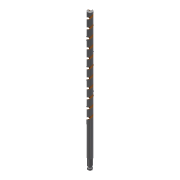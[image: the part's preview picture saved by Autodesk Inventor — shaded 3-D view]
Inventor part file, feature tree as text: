
AUTODESK INVENTOR PART (.ipt)
format: ipt  version: 2014 SP1 (Build 180222100, 222)  size: 258,048 bytes
history: native  units: in
note: dims shown in document units (in); Inventor stores cm internally (conversion verified against a paired STEP export)
features: sketch x6, extrude x4, fillet x1, helix x1
ambient origin geometry x8: Origin, YZ Plane, XZ Plane, XY Plane, X Axis, Y Axis, Z Axis, Center Point
bodies: Solid1 (feature_tree)
feature tree (12):
  extrude  "Extrusion1"  Depth=0.21in TaperAngle=0.0deg
  extrude  "Extrusion2"  Depth=0.1805in TaperAngle=0.0deg
  extrude  "Extrusion3"  Depth=0.89in TaperAngle=0.0deg
  fillet  "Fillet1"  Radius=0.05in
  extrude  "Extrusion4"  Depth=16.0in TaperAngle=0.0deg
  sketch  "Sketch5"  dims[d13=1.0in d14=12.0in d15=4.3307in d16=0.0in d17=90.0deg d18=90.0deg d19=0.0in d20=0.0in]
  sketch  "Sketch6"
  helix  "Coil1"  [1 undecoded]
  sketch  "Sketch1"  dims[d0=0.463in d1=0.21in d2=0.0in]
  sketch  "Sketch2"  dims[d3=0.348in d4=0.1805in d5=0.0in]
  sketch  "Sketch3"  dims[d6=0.463in d7=0.89in d8=0.0in d9=0.05in]
  sketch  "Sketch4"  dims[d10=0.625in d11=16.0in d12=0.0in]
note: 1 required parameter value undecoded (feature->parameter linkage not recoverable at this tier; creation-order binding heuristic only, values carry confidence <= 0.55)
